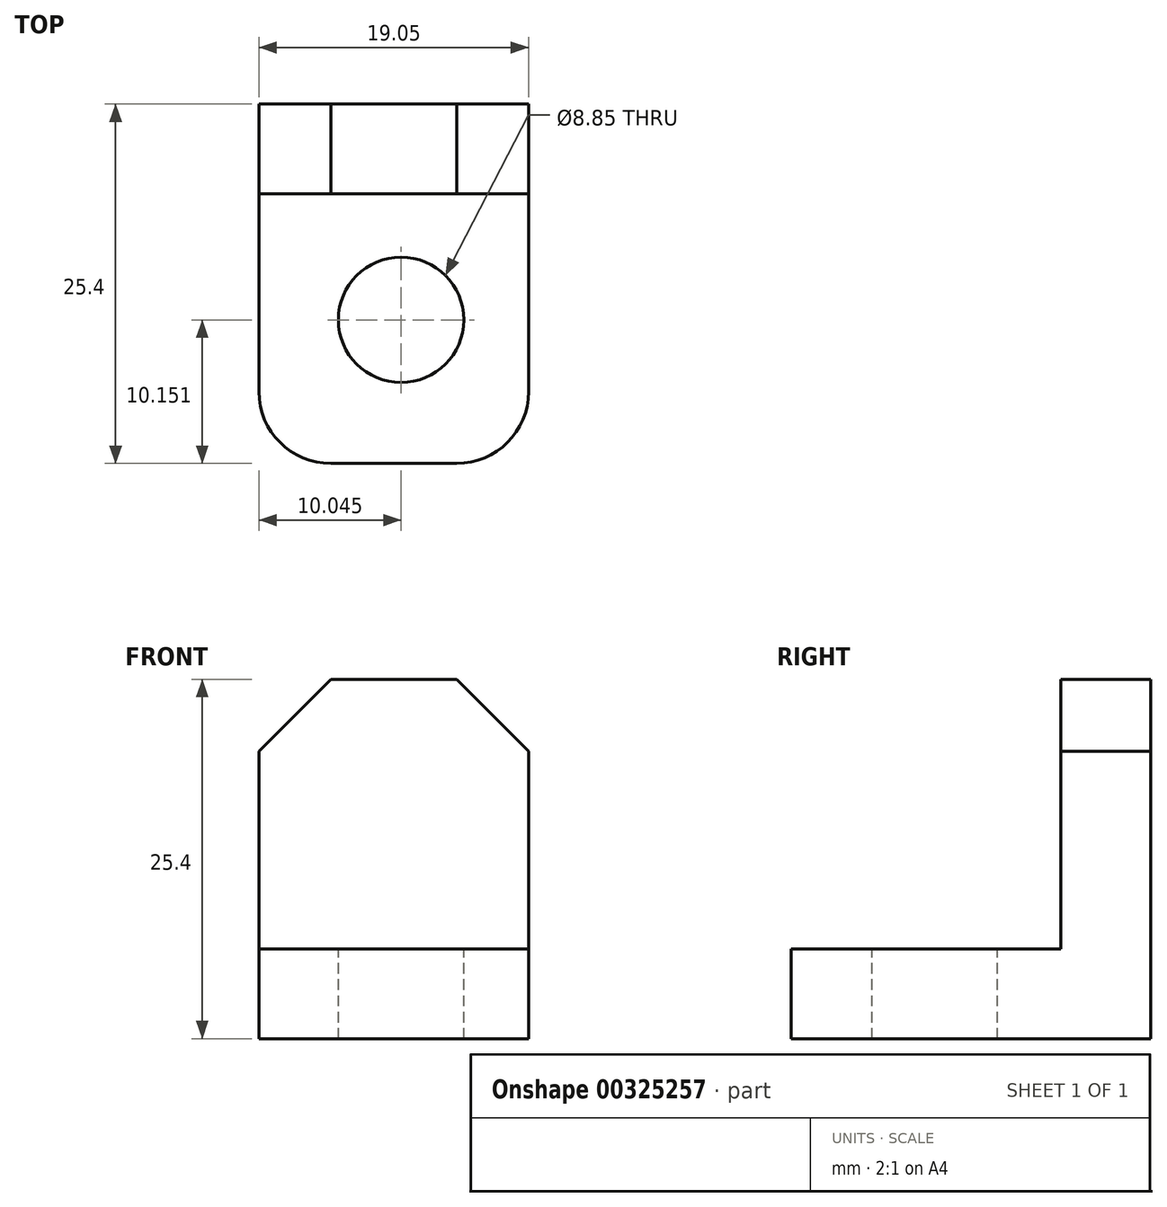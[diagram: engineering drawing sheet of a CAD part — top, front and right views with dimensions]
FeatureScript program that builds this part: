
annotation { "Feature Type Name" : "Feature", "Feature Type Description" : "" }
export const myFeature = defineFeature(function(context is Context, id is Id, definition is map)
    precondition{}
    {
        {
            var Q0;
            Q0=qCreatedBy(makeId("Front.planeOp"),FACE);
            var sketch = newSketch(context, id + "F0", { "sketchPlane" : qUnion([Q0])});
            skLineSegment(sketch, "E0.bottom", {"start": v(-33.03, 28.04) * mm, "end": v(-13.98, 28.04) * mm});
            skLineSegment(sketch, "E0.top", {"start": v(-33.03, 8.99) * mm, "end": v(-13.98, 8.99) * mm});
            skLineSegment(sketch, "E0.left", {"start": v(-33.03, 28.04) * mm, "end": v(-33.03, 8.99) * mm});
            skLineSegment(sketch, "E0.right", {"start": v(-13.98, 28.04) * mm, "end": v(-13.98, 8.99) * mm});
            skSolve(sketch);
        }
        {
            var Q0;
            Q0=makeQuery(id+"F0.imprint","IMPRINT",FACE,{"disambiguationData":[TD([[makeQuery(id+"F0.imprint","IMPRINT",EDGE,{"derivedFrom":sQuery(id+"F0.wireOp",EDGE,"E0.bottom")}),-1.0]])]});
            extrude(context, id + "F1", {"entities" : qUnion([Q0]), "depth" : 6.35 * mm});
        }
        {
            var Q0;
            Q0=makeQuery(id+"F1.opExtrude","SWEPT_FACE",FACE,{"disambiguationData":[OSD([sQuery(id+"F0.wireOp",EDGE,"E0.top")])]});
            var sketch = newSketch(context, id + "F2", { "sketchPlane" : qUnion([Q0])});
            skLineSegment(sketch, "E1.bottom", {"start": v(-33.03, 0) * mm, "end": v(-13.98, 0) * mm});
            skLineSegment(sketch, "E1.top", {"start": v(-33.03, 25.4) * mm, "end": v(-13.98, 25.4) * mm});
            skLineSegment(sketch, "E1.left", {"start": v(-33.03, 0) * mm, "end": v(-33.03, 25.4) * mm});
            skLineSegment(sketch, "E1.right", {"start": v(-13.98, 0) * mm, "end": v(-13.98, 25.4) * mm});
            skSolve(sketch);
        }
        {
            var Q0;
            Q0 = qSketchRegion(id + "F2", true);
            extrude(context, id + "F3", {"entities" : qUnion([Q0]), "operationType" : NewBodyOperationType.ADD, "depth" : 6.35 * mm});
        }
        {
            var Q0;
            Q0=makeQuery(id+"F3.opExtrude","SWEPT_EDGE",EDGE,{"disambiguationData":[OSD([sQuery(id+"F2.wireOp",EDGE,"E1.top"),sQuery(id+"F2.wireOp",EDGE,"E1.right")])]});
            fillet(context, id + "F4", {"entities" : qUnion([Q0]), "radius" : 5.08 * mm, "tangentPropagation" : true, "allowEdgeOverflow" : false});
        }
        {
            var Q0;
            Q0=makeQuery(id+"F3.opExtrude","SWEPT_EDGE",EDGE,{"disambiguationData":[OSD([sQuery(id+"F2.wireOp",EDGE,"E1.top"),sQuery(id+"F2.wireOp",EDGE,"E1.left")])]});
            fillet(context, id + "F5", {"entities" : qUnion([Q0]), "radius" : 5.08 * mm, "tangentPropagation" : true, "allowEdgeOverflow" : false});
        }
        {
            var Q0;
            Q0=makeQuery(id+"F1.opExtrude","SWEPT_EDGE",EDGE,{"disambiguationData":[OSD([sQuery(id+"F0.wireOp",EDGE,"E0.bottom"),sQuery(id+"F0.wireOp",EDGE,"E0.right")])]});
            var Q1;
            Q1=makeQuery(id+"F1.opExtrude","SWEPT_EDGE",EDGE,{"disambiguationData":[OSD([sQuery(id+"F0.wireOp",EDGE,"E0.bottom"),sQuery(id+"F0.wireOp",EDGE,"E0.left")])]});
            chamfer(context, id + "F6", {"entities" : qUnion([Q0, Q1]), "width" : 5.08 * mm, "tangentPropagation" : true});
        }
        {
            var Q0;
            Q0=makeQuery(id+"F3.opExtrude","CAP_FACE",FACE,{"disambiguationData":[OSD([sQuery(id+"F2.wireOp",EDGE,"E1.bottom"),sQuery(id+"F2.wireOp",EDGE,"E1.top"),sQuery(id+"F2.wireOp",EDGE,"E1.left"),sQuery(id+"F2.wireOp",EDGE,"E1.right")])],"isStart":true});
            var sketch = newSketch(context, id + "F7", { "sketchPlane" : qUnion([Q0])});
            skCircle(sketch, "E2", {"center": v(-22.99, -15.25) * mm, "radius": 4.43 * mm});
            skSolve(sketch);
        }
        {
            var Q0;
            Q0=makeQuery(id+"F7.imprint","IMPRINT",FACE,{"disambiguationData":[TD([[makeQuery(id+"F7.imprint","IMPRINT",EDGE,{"derivedFrom":sQuery(id+"F7.wireOp",EDGE,"E2")}),1.0]])]});
            extrude(context, id + "F8", {"entities" : qUnion([Q0]), "operationType" : NewBodyOperationType.REMOVE, "endBound" : BoundingType.THROUGH_ALL, "oppositeDirection" : true, "depth" : 6.6 * mm});
        }
    });
